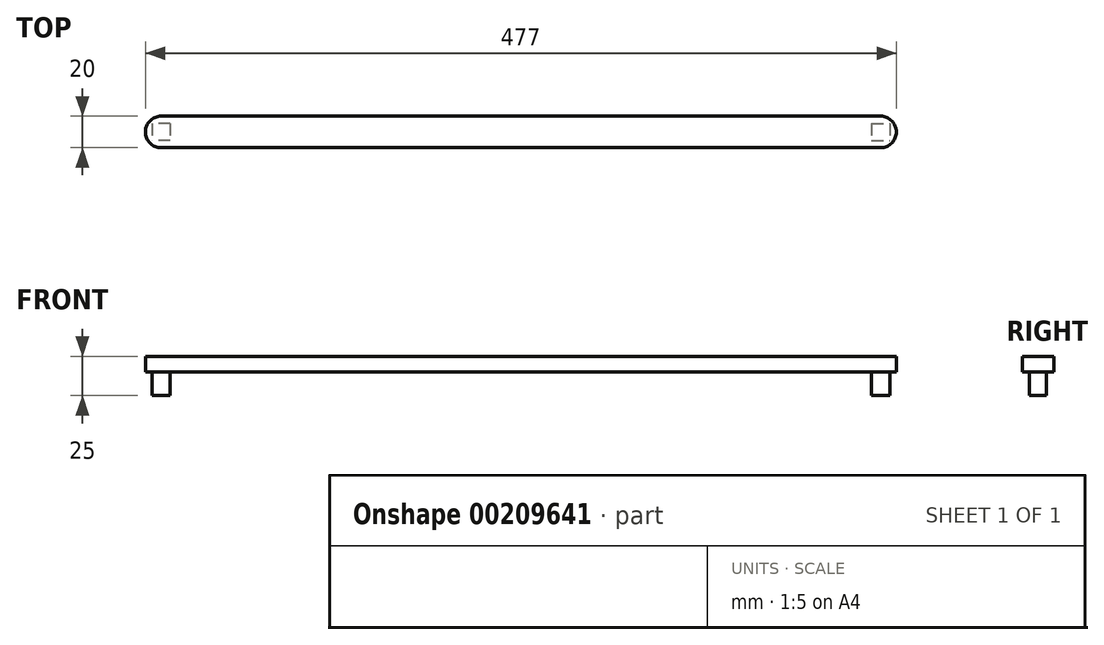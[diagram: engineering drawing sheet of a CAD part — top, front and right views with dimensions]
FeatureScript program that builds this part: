
annotation { "Feature Type Name" : "Feature", "Feature Type Description" : "" }
export const myFeature = defineFeature(function(context is Context, id is Id, definition is map)
    precondition{}
    {
        {
            var Q0;
            Q0=qCreatedBy(makeId("Top.planeOp"),FACE);
            var sketch = newSketch(context, id + "F0", { "sketchPlane" : qUnion([Q0])});
            skLineSegment(sketch, "E0.bottom", {"start": v(18.7, 54.43) * mm, "end": v(475.7, 54.43) * mm});
            skLineSegment(sketch, "E0.top", {"start": v(18.7, 34.43) * mm, "end": v(475.7, 34.43) * mm});
            skCircle(sketch, "E1", {"center": v(18.7, 44.43) * mm, "radius": 5 * mm});
            skPoint(sketch, "E1.centerSnap0", {"position": v(38.7, 44.43) * mm});
            skCircle(sketch, "E2", {"center": v(475.7, 44.43) * mm, "radius": 5 * mm});
            skLineSegment(sketch, "E3.bottom", {"start": v(195.5, 471.98) * mm, "end": v(645.5, 471.98) * mm});
            skLineSegment(sketch, "E3.top", {"start": v(195.5, 121.98) * mm, "end": v(645.5, 121.98) * mm});
            skLineSegment(sketch, "E3.left", {"start": v(195.5, 471.98) * mm, "end": v(195.5, 121.98) * mm});
            skLineSegment(sketch, "E3.right", {"start": v(645.5, 471.98) * mm, "end": v(645.5, 121.98) * mm});
            skLineSegment(sketch, "E4", {"start": v(360.5, 471.98) * mm, "end": v(362.84, 307) * mm});
            skArc(sketch, "E5", {"start": v(18.7, 54.43) * mm, "mid": v(8.7, 44.43) * mm, "end": v(18.7, 34.43) * mm});
            skArc(sketch, "E6", {"start": v(475.7, 54.43) * mm, "mid": v(485.7, 44.43) * mm, "end": v(475.7, 34.43) * mm});
            skPoint(sketch, "E7.orphan", {"position": v(38.7, 54.43) * mm});
            skPoint(sketch, "E0.left.end.orphan", {"position": v(38.7, 34.43) * mm});
            skLineSegment(sketch, "E8", {"start": v(247.2, 15.14) * mm, "end": v(247.2, -23.5) * mm, "construction": true});
            skPoint(sketch, "E8.startSnap0", {"position": v(247.2, 34.43) * mm});
            skSolve(sketch);
        }
        {
            var Q0;
            Q0=makeQuery(id+"F0.imprint","IMPRINT",FACE,{"disambiguationData":[TD([[makeQuery(id+"F0.imprint","IMPRINT",EDGE,{"derivedFrom":sQuery(id+"F0.wireOp",EDGE,"E0.bottom")}),-1.0]])]});
            extrude(context, id + "F1", {"entities" : qUnion([Q0]), "depth" : 10 * mm});
        }
        {
            var Q0;
            Q0=qCreatedBy(makeId("Top.planeOp"),FACE);
            var sketch = newSketch(context, id + "F2", { "sketchPlane" : qUnion([Q0])});
            skLineSegment(sketch, "E9.bottom", {"start": v(24.52, 49.8) * mm, "end": v(12.87, 49.8) * mm});
            skLineSegment(sketch, "E9.top", {"start": v(24.52, 39.05) * mm, "end": v(12.87, 39.05) * mm});
            skLineSegment(sketch, "E9.left", {"start": v(24.52, 49.8) * mm, "end": v(24.52, 39.05) * mm});
            skLineSegment(sketch, "E9.right", {"start": v(12.87, 49.8) * mm, "end": v(12.87, 39.05) * mm});
            skPoint(sketch, "E9.middle", {"position": v(18.7, 44.43) * mm});
            skLineSegment(sketch, "E10.MirrorCS", {"start": v(469.87, 49.8) * mm, "end": v(469.87, 39.05) * mm});
            skLineSegment(sketch, "E11.MirrorCS", {"start": v(469.87, 39.05) * mm, "end": v(481.52, 39.05) * mm});
            skLineSegment(sketch, "E12.MirrorCS", {"start": v(481.52, 49.8) * mm, "end": v(481.52, 39.05) * mm});
            skLineSegment(sketch, "E13.MirrorCS", {"start": v(469.87, 49.8) * mm, "end": v(481.52, 49.8) * mm});
            skSolve(sketch);
        }
        {
            var Q0;
            Q0=makeQuery(id+"F2.imprint","IMPRINT",FACE,{"disambiguationData":[TD([[makeQuery(id+"F2.imprint","IMPRINT",EDGE,{"derivedFrom":sQuery(id+"F2.wireOp",EDGE,"E9.bottom")}),1.0]])]});
            var Q1;
            Q1=makeQuery(id+"F2.imprint","IMPRINT",FACE,{"disambiguationData":[TD([[makeQuery(id+"F2.imprint","IMPRINT",EDGE,{"derivedFrom":sQuery(id+"F2.wireOp",EDGE,"E10.MirrorCS")}),1.0]])]});
            extrude(context, id + "F3", {"entities" : qUnion([Q0, Q1]), "oppositeDirection" : true, "depth" : 15 * mm});
        }
        {
            var Q0;
            Q0=makeQuery(id+"F0.imprint","IMPRINT",FACE,{"disambiguationData":[TD([[makeQuery(id+"F0.imprint","IMPRINT",EDGE,{"derivedFrom":sQuery(id+"F0.wireOp",EDGE,"E1")}),1.0]])]});
            var Q1;
            Q1=makeQuery(id+"F0.imprint","IMPRINT",FACE,{"disambiguationData":[TD([[makeQuery(id+"F0.imprint","IMPRINT",EDGE,{"derivedFrom":sQuery(id+"F0.wireOp",EDGE,"E2")}),1.0]])]});
            extrude(context, id + "F4", {"entities" : qUnion([Q0, Q1]), "operationType" : NewBodyOperationType.ADD, "depth" : 10 * mm});
        }
    });
